# Revit family: IS_ConceptAir_Multiproduct_BIM_GB_E0826;E0827;E0828;E0829
name_source: partatom
category: Plumbing Fixtures
revit_build: Autodesk Revit MEP 2014 (Build: 20140709_2115(x64)
units: mm (PartAtom-declared; Revit-internal decimal feet)

## types (24) — shared parameters
Accessories = www.idealspec.co.uk
AreaUnits = millimeters
Assembly Code = C1030200
AssetType = Fixed
BREEAM = No
Brand = IdealStandard
Default Elevation = 800 mm  [stored 2.62467 ft]
DurationUnit = year
ECA = No
ExpectedLife = 30
IfcExportAs = IfcFurnitureType
IfcExportType = USERDEFINED
InstallationInstructions = www.idealspec.co.uk/resources.html
LinearUnits = millimeters
ManufacturerURL = www.idealspec.co.uk
Material = Laquered MDF
NBSDescription = Bathroom integrated duct work
NBSReference = 45-35-72/320
NettWeight = 0 Kg
NominalDepth = 440 mm  [stored 1.44357 ft]
NominalHeight = 517 mm  [stored 1.69619 ft]
NominalLength = 440 mm  [stored 1.44357 ft]
Shape = Rectangular
Space = Internal
SpareParts = www.fastpart-spares.co.uk
TMV3 = No
URL = www.idealspec.co.uk
Uniclass2 = Pr_40_30_78_04
Version = 1
VolumeUnits = Litres
WRAS = No
WarrantyDescription = Manufacturers warranty
WarrantyDurationParts = 5
WarrantyDurationUnit = year
WaterEfficientProduct = No
zero-valued in all types: CWFU, Cost, HWFU, WFU

## per-type parameters (varying)
| type | 1Drawer | 2Drawer | BIMObjectName | Color | Description | Features | Finish | InnerColour | MainColor | MainColour | Model | ModelNumber | ModelReference | Name | NominalWidth | ProductInformation | Size |
| E0828B2 - 100CM Wall Hung Vanity Unit 1 Drawer with open shelf Gls White + Matt White | Yes | No | ISI_IdealStandard_Furniture_ConceptAir_E0828B2 | White | Concept Air 100 cm Wall Hung Vanity Unit 1 Drawer with open shelf Gls White + Matt White | 100 cm Wall Hung Vanity Unit 1 Drawer with open shelf Gls White + Matt White | White | ISI_IdealStandard_Laminate_White_Render | White | ISI_IdealStandard_Laminate_White_Render | E0828B2 | E0828B2 | Concept Air 100 cm Wall Hung Vanity Unit 1 Drawer with open shelf Gls White + Matt White | Furniture_ConceptAir_E0828B2_IdealStandard | 1000 mm  [stored 3.28084 ft] | www.idealspec.co.uk/assets/datasheet/E0828B2 | 517 x 440 x 1000 mm |
| E0828UK - 100CM Wall Hung Vanity Unit 1 Drawer with open shelf Wood Light Brown + Matt Light Brown | Yes | No | ISI_IdealStandard_Furniture_ConceptAir_E0828UK | Wood brown | Concept Air 100 cm Wall Hung Vanity Unit 1 Drawer with open shelf Wood Light Brown + Matt Light Brown | 100 cm Wall Hung Vanity Unit 1 Drawer with open shelf Wood Light Brown + Matt Light Brown | Wood brown | ISI_IdealStandard_Furniture_WoodLightBrown_Render | Wood brown | ISI_IdealStandard_Furniture_WoodLightBrown_Render | E0828UK | E0828UK | Concept Air 100 cm Wall Hung Vanity Unit 1 Drawer with open shelf Wood Light Brown + Matt Light Brown | Furniture_ConceptAir_E0828UK_IdealStandard | 1000 mm  [stored 3.28084 ft] | www.idealspec.co.uk/assets/datasheet/E0828UK | 517 x 440 x 1000 mm |
| E0828PS - 100CM Wall Hung Vanity Unit 1 Drawer with open shelf Wood Light Grey + Matt White | Yes | No | ISI_IdealStandard_Furniture_ConceptAir_E0828PS | Wood grey | Concept Air 100 cm Wall Hung Vanity Unit 1 Drawer with open shelf Wood Light Grey + Matt White | 100 cm Wall Hung Vanity Unit 1 Drawer with open shelf Wood Light Grey + Matt White | Wood grey | ISI_IdealStandard_Laminate_White_Render | Wood grey | ISI_IdealStandard_Furniture_WoodLightGrey_Render | E0828PS | E0828PS | Concept Air 100 cm Wall Hung Vanity Unit 1 Drawer with open shelf Wood Light Grey + Matt White | Furniture_ConceptAir_E0828PS_IdealStandard | 1000 mm  [stored 3.28084 ft] | www.idealspec.co.uk/assets/datasheet/E0828PS | 517 x 440 x 1000 mm |
| E0828KN - 100CM Wall Hung Vanity Unit 1 Drawer with open shelf Gls White + Matt Light Grey | Yes | No | ISI_IdealStandard_Furniture_ConceptAir_E0828KN | White | Concept Air 100 cm Wall Hung Vanity Unit 1 Drawer with open shelf Gls White + Matt Light Grey | 100 cm Wall Hung Vanity Unit 1 Drawer with open shelf Gls White + Matt Light Grey | White | ISI_IdealStandard_Furniture_Grey_Render | White | ISI_IdealStandard_Laminate_White_Render | E0828KN | E0828KN | Concept Air 100 cm Wall Hung Vanity Unit 1 Drawer with open shelf Gls White + Matt Light Grey | Furniture_ConceptAir_E0828KN_IdealStandard | 1000 mm  [stored 3.28084 ft] | www.idealspec.co.uk/assets/datasheet/E0828KN | 517 x 440 x 1000 mm |
| E0827EQ - 80CM Wall Hung Vanity Unit 1 Drawer with open shelf Gls Light Grey + Matt White | Yes | No | ISI_IdealStandard_Furniture_ConceptAir_E0827EQ | Grey | Concept Air 80 cm Wall Hung Vanity Unit 1 Drawer with open shelf Gls Light Grey + Matt White | 80 cm Wall Hung Vanity Unit 1 Drawer with open shelf Gls Light Grey + Matt White | Grey | ISI_IdealStandard_Laminate_White_Render | Grey | ISI_IdealStandard_Furniture_Grey_Render | E0827EQ | E0827EQ | Concept Air 80 cm Wall Hung Vanity Unit 1 Drawer with open shelf Gls Light Grey + Matt White | Furniture_ConceptAir_E0827EQ_IdealStandard | 800 mm  [stored 2.62467 ft] | www.idealspec.co.uk/assets/datasheet/E0827EQ | 517 x 440 x 800 mm |
| E0827UK - 80CM Wall Hung Vanity Unit 1 Drawer with open shelf Wood Light Brown + Matt Light Brown | Yes | No | ISI_IdealStandard_Furniture_ConceptAir_E0827UK | Wood brown | Concept Air 80 cm Wall Hung Vanity Unit 1 Drawer with open shelf Wood Light Brown + Matt Light Brown | 80 cm Wall Hung Vanity Unit 1 Drawer with open shelf Wood Light Brown + Matt Light Brown | Wood brown | ISI_IdealStandard_Furniture_WoodLightBrown_Render | Wood brown | ISI_IdealStandard_Furniture_WoodLightBrown_Render | E0827UK | E0827UK | Concept Air 80 cm Wall Hung Vanity Unit 1 Drawer with open shelf Wood Light Brown + Matt Light Brown | Furniture_ConceptAir_E0827UK_IdealStandard | 800 mm  [stored 2.62467 ft] | www.idealspec.co.uk/assets/datasheet/E0827UK | 517 x 440 x 800 mm |
| E0827PS - 80CM Wall Hung Vanity Unit 1 Drawer with open shelf Wood Light Grey + Matt White | Yes | No | ISI_IdealStandard_Furniture_ConceptAir_E0827PS | Wood grey | Concept Air 80 cm Wall Hung Vanity Unit 1 Drawer with open shelf Wood Light Grey + Matt White | 80 cm Wall Hung Vanity Unit 1 Drawer with open shelf Wood Light Grey + Matt White | Wood grey | ISI_IdealStandard_Laminate_White_Render | Wood grey | ISI_IdealStandard_Furniture_WoodLightGrey_Render | E0827PS | E0827PS | Concept Air 80 cm Wall Hung Vanity Unit 1 Drawer with open shelf Wood Light Grey + Matt White | Furniture_ConceptAir_E0827PS_IdealStandard | 800 mm  [stored 2.62467 ft] | www.idealspec.co.uk/assets/datasheet/E0827PS | 517 x 440 x 800 mm |
| E0827KN - 80CM Wall Hung Vanity Unit 1 Drawer with open shelf Gls White + Matt Light Grey | Yes | No | ISI_IdealStandard_Furniture_ConceptAir_E0827KN | White | Concept Air 80 cm Wall Hung Vanity Unit 1 Drawer with open shelf Gls White + Matt Light Grey | 80 cm Wall Hung Vanity Unit 1 Drawer with open shelf Gls White + Matt Light Grey | White | ISI_IdealStandard_Furniture_Grey_Render | White | ISI_IdealStandard_Laminate_White_Render | E0827KN | E0827KN | Concept Air 80 cm Wall Hung Vanity Unit 1 Drawer with open shelf Gls White + Matt Light Grey | Furniture_ConceptAir_E0827KN_IdealStandard | 800 mm  [stored 2.62467 ft] | www.idealspec.co.uk/assets/datasheet/E0827KN | 517 x 440 x 800 mm |
| E0828EQ - 100CM Wall Hung Vanity Unit 1 Drawer with open shelf Gls Light Grey + Matt White | Yes | No | ISI_IdealStandard_Furniture_ConceptAir_E0828EQ | Grey | Concept Air 100 cm Wall Hung Vanity Unit 1 Drawer with open shelf Gls Light Grey + Matt White | 100 cm Wall Hung Vanity Unit 1 Drawer with open shelf Gls Light Grey + Matt White | Grey | ISI_IdealStandard_Laminate_White_Render | Grey | ISI_IdealStandard_Furniture_Grey_Render | E0828EQ | E0828EQ | Concept Air 100 cm Wall Hung Vanity Unit 1 Drawer with open shelf Gls Light Grey + Matt White | Furniture_ConceptAir_E0828EQ_IdealStandard | 1000 mm  [stored 3.28084 ft] | www.idealspec.co.uk/assets/datasheet/E0828EQ | 517 x 440 x 1000 mm |
| E0827B2 - 80CM Wall Hung Vanity Unit 1 Drawer with open shelf Gls White + Matt White | Yes | No | ISI_IdealStandard_Furniture_ConceptAir_E0827B2 | White | Concept Air 80 cm Wall Hung Vanity Unit 1 Drawer with open shelf Gls White + Matt White | 80 cm Wall Hung Vanity Unit 1 Drawer with open shelf Gls White + Matt White | White | ISI_IdealStandard_Laminate_White_Render | White | ISI_IdealStandard_Laminate_White_Render | E0827B2 | E0827B2 | Concept Air 80 cm Wall Hung Vanity Unit 1 Drawer with open shelf Gls White + Matt White | Furniture_ConceptAir_E0827B2_IdealStandard | 800 mm  [stored 2.62467 ft] | www.idealspec.co.uk/assets/datasheet/E0827B2 | 517 x 440 x 800 mm |
| E0826UK - 60CM Wall Hung Vanity Unit 1 Drawer with open shelf Wood Light Brown + Matt Light Brown | Yes | No | ISI_IdealStandard_Furniture_ConceptAir_E0826UK | Wood brown | Concept Air 60 cm Wall Hung Vanity Unit 1 Drawer with open shelf Wood Light Brown + Matt Light Brown | 60 cm Wall Hung Vanity Unit 1 Drawer with open shelf Wood Light Brown + Matt Light Brown | Wood brown | ISI_IdealStandard_Furniture_WoodLightBrown_Render | Wood brown | ISI_IdealStandard_Furniture_WoodLightBrown_Render | E0826UK | E0826UK | Concept Air 60 cm Wall Hung Vanity Unit 1 Drawer with open shelf Wood Light Brown + Matt Light Brown | Furniture_ConceptAir_E0826UK_IdealStandard | 600 mm | www.idealspec.co.uk/assets/datasheet/E0826UK | 517 x 440 x 600 mm |
| E0826PS - 60CM Wall Hung Vanity Unit 1 Drawer with open shelf Wood Light Grey + Matt White | Yes | No | ISI_IdealStandard_Furniture_ConceptAir_E0826PS | Wood grey | Concept Air 60 cm Wall Hung Vanity Unit 1 Drawer with open shelf Wood Light Grey + Matt White | 60 cm Wall Hung Vanity Unit 1 Drawer with open shelf Wood Light Grey + Matt White | Wood grey | ISI_IdealStandard_Laminate_White_Render | Wood grey | ISI_IdealStandard_Furniture_WoodLightGrey_Render | E0826PS | E0826PS | Concept Air 60 cm Wall Hung Vanity Unit 1 Drawer with open shelf Wood Light Grey + Matt White | Furniture_ConceptAir_E0826PS_IdealStandard | 600 mm | www.idealspec.co.uk/assets/datasheet/E0826PS | 517 x 440 x 600 mm |
| E0826KN - 60CM Wall Hung Vanity Unit 1 Drawer with open shelf Gls White + Matt Light Grey | Yes | No | ISI_IdealStandard_Furniture_ConceptAir_E0826KN | White | Concept Air 60 cm Wall Hung Vanity Unit 1 Drawer with open shelf Gls White + Matt Light Grey | 60 cm Wall Hung Vanity Unit 1 Drawer with open shelf Gls White + Matt Light Grey | White | ISI_IdealStandard_Furniture_Grey_Render | White | ISI_IdealStandard_Laminate_White_Render | E0826KN | E0826KN | Concept Air 60 cm Wall Hung Vanity Unit 1 Drawer with open shelf Gls White + Matt Light Grey | Furniture_ConceptAir_E0826KN_IdealStandard | 600 mm | www.idealspec.co.uk/assets/datasheet/E0826KN | 517 x 440 x 600 mm |
| E0826EQ - 60CM Wall Hung Vanity Unit 1 Drawer with open shelf Gls Light Grey + Matt White | Yes | No | ISI_IdealStandard_Furniture_ConceptAir_E0826EQ | Grey | Concept Air 60 cm Wall Hung Vanity Unit 1 Drawer with open shelf Gls Light Grey + Matt White | 60 cm Wall Hung Vanity Unit 1 Drawer with open shelf Gls Light Grey + Matt White | Grey | ISI_IdealStandard_Laminate_White_Render | Grey | ISI_IdealStandard_Furniture_Grey_Render | E0826EQ | E0826EQ | Concept Air 60 cm Wall Hung Vanity Unit 1 Drawer with open shelf Gls Light Grey + Matt White | Furniture_ConceptAir_E0826EQ_IdealStandard | 600 mm | www.idealspec.co.uk/assets/datasheet/E0826EQ | 517 x 440 x 600 mm |
| E0826B2 - 60CM Wall Hung Vanity Unit 1 Drawer with open shelf Gls White + Matt White | Yes | No | ISI_IdealStandard_Furniture_ConceptAir_E0826B2 | White | Concept Air 60 cm Wall Hung Vanity Unit 1 Drawer with open shelf Gls White + Matt White | 60 cm Wall Hung Vanity Unit 1 Drawer with open shelf Gls White + Matt White | White | ISI_IdealStandard_Laminate_White_Render | White | ISI_IdealStandard_Laminate_White_Render | E0826B2 | E0826B2 | Concept Air 60 cm Wall Hung Vanity Unit 1 Drawer with open shelf Gls White + Matt White | Furniture_ConceptAir_E0826B2_IdealStandard | 600 mm | www.idealspec.co.uk/assets/datasheet/E0826B2 | 517 x 440 x 600 mm |
| E0829B2 - 120CM Wall Hung Vanity Unit 2 Drawer with open shelf Gls White + Matt White | No | Yes | ISI_IdealStandard_Furniture_ConceptAir_E0829B2 | White | Concept Air 120 cm Wall Hung Vanity Unit 2 Drawer with open shelf Gls White + Matt White | 120 cm Wall Hung Vanity Unit 2 Drawer with open shelf Gls White + Matt White | White | ISI_IdealStandard_Laminate_White_Render | White | ISI_IdealStandard_Laminate_White_Render | E0829B2 | E0829B2 | Concept Air 120 cm Wall Hung Vanity Unit 2 Drawer with open shelf Gls White + Matt White | Furniture_ConceptAir_E0829B2_IdealStandard | 1200 mm | www.idealspec.co.uk/assets/datasheet/E0829B2 | 517 x 440 x 1200 mm |
| E0829EQ - 120CM Wall Hung Vanity Unit 2 Drawer with open shelf Gls Light Grey + Matt White | No | Yes | ISI_IdealStandard_Furniture_ConceptAir_E0829EQ | Grey | Concept Air 120 cm Wall Hung Vanity Unit 2 Drawer with open shelf Gls Light Grey + Matt White | 120 cm Wall Hung Vanity Unit 2 Drawer with open shelf Gls Light Grey + Matt White | Grey | ISI_IdealStandard_Laminate_White_Render | Grey | ISI_IdealStandard_Furniture_Grey_Render | E0829EQ | E0829EQ | Concept Air 120 cm Wall Hung Vanity Unit 2 Drawer with open shelf Gls Light Grey + Matt White | Furniture_ConceptAir_E0829EQ_IdealStandard | 1200 mm | www.idealspec.co.uk/assets/datasheet/E0829EQ | 517 x 440 x 1200 mm |
| E0829KN - 120CM Wall Hung Vanity Unit 2 Drawer with open shelf Gls White + Matt Light Grey | No | Yes | ISI_IdealStandard_Furniture_ConceptAir_E0829KN | White | Concept Air 120 cm Wall Hung Vanity Unit 2 Drawer with open shelf Gls White + Matt Light Grey | 120 cm Wall Hung Vanity Unit 2 Drawer with open shelf Gls White + Matt Light Grey | White | ISI_IdealStandard_Furniture_Grey_Render | White | ISI_IdealStandard_Laminate_White_Render | E0829KN | E0829KN | Concept Air 120 cm Wall Hung Vanity Unit 2 Drawer with open shelf Gls White + Matt Light Grey | Furniture_ConceptAir_E0829KN_IdealStandard | 1200 mm | www.idealspec.co.uk/assets/datasheet/E0829KN | 517 x 440 x 1200 mm |
| E0829PS - 120CM Wall Hung Vanity Unit 2 Drawer with open shelf Wood Light Grey + Matt White | No | Yes | ISI_IdealStandard_Furniture_ConceptAir_E0829PS | Wood grey | Concept Air 120 cm Wall Hung Vanity Unit 2 Drawer with open shelf Wood Light Grey + Matt White | 120 cm Wall Hung Vanity Unit 2 Drawer with open shelf Wood Light Grey + Matt White | Wood grey | ISI_IdealStandard_Laminate_White_Render | Wood grey | ISI_IdealStandard_Furniture_WoodLightGrey_Render | E0829PS | E0829PS | Concept Air 120 cm Wall Hung Vanity Unit 2 Drawer with open shelf Wood Light Grey + Matt White | Furniture_ConceptAir_E0829PS_IdealStandard | 1200 mm | www.idealspec.co.uk/assets/datasheet/E0829PS | 517 x 440 x 1200 mm |
| E0829UK - 120CM Wall Hung Vanity Unit 2 Drawer with open shelf Wood Light Brown + Matt Light Brown | No | Yes | ISI_IdealStandard_Furniture_ConceptAir_E0829UK | Wood brown | Concept Air 120 cm Wall Hung Vanity Unit 2 Drawer with open shelf Wood Light Brown + Matt Light Brown | 120 cm Wall Hung Vanity Unit 2 Drawer with open shelf Wood Light Brown + Matt Light Brown | Wood brown | ISI_IdealStandard_Furniture_WoodLightBrown_Render | Wood brown | ISI_IdealStandard_Furniture_WoodLightBrown_Render | E0829UK | E0829UK | Concept Air 120 cm Wall Hung Vanity Unit 2 Drawer with open shelf Wood Light Brown + Matt Light Brown | Furniture_ConceptAir_E0829UK_IdealStandard | 1200 mm | www.idealspec.co.uk/assets/datasheet/E0829UK | 517 x 440 x 1200 mm |
| E0829VY - 120CM Wall Hung Vanity Unit 2 Drawer with open shelf Matt Dark Brown + Matt White | No | Yes | ISI_IdealStandard_Furniture_ConceptAir_E0829VY | Dark brown | Concept Air 120 cm Wall Hung Vanity Unit 2 Drawer with open shelf Matt Dark Brown + Matt White | 120 cm Wall Hung Vanity Unit 2 Drawer with open shelf Matt Dark Brown + Matt White | Dark brown | ISI_IdealStandard_Laminate_White_Render | Dark brown | ISI_IdealStandard_Furniture_DarkBrown_Render | E0829VY | E0829VY | Concept Air 120 cm Wall Hung Vanity Unit 2 Drawer with open shelf Gls Dark Brown + Matt White | Furniture_ConceptAir_E0829VY_IdealStandard | 1200 mm | www.idealspec.co.uk/assets/datasheet/E0829VY | 517 x 440 x 1200 mm |
| E0826VY - 60CM Wall Hung Vanity Unit 1 Drawer with open shelf Matt Dark Brown + Matt White | Yes | No | ISI_IdealStandard_Furniture_ConceptAir_E0826VY | Dark brown | Concept Air 60 cm Wall Hung Vanity Unit 1 Drawer with open shelf Matt Dark Brown + Matt White | 60 cm Wall Hung Vanity Unit 1 Drawer with open shelf Matt Dark Brown + Matt White | Dark brown | ISI_IdealStandard_Laminate_White_Render | Dark brown | ISI_IdealStandard_Furniture_DarkBrown_Render | E0826VY | E0826VY | Concept Air 60 cm Wall Hung Vanity Unit 1 Drawer with open shelf Gls Dark Brown + Matt White | Furniture_ConceptAir_E0826VY_IdealStandard | 600 mm | www.idealspec.co.uk/assets/datasheet/E0826VY | 517 x 440 x 600 mm |
| E0827VY - 80CM Wall Hung Vanity Unit 1 Drawer with open shelf Matt Dark Brown + Matt White | Yes | No | ISI_IdealStandard_Furniture_ConceptAir_E0827VY | Dark brown | Concept Air 80 cm Wall Hung Vanity Unit 1 Drawer with open shelf Matt Dark Brown + Matt White | 80 cm Wall Hung Vanity Unit 1 Drawer with open shelf Matt Dark Brown + Matt White | Dark brown | ISI_IdealStandard_Laminate_White_Render | Dark brown | ISI_IdealStandard_Furniture_DarkBrown_Render | E0827VY | E0827VY | Concept Air 80 cm Wall Hung Vanity Unit 1 Drawer with open shelf Gls Dark Brown + Matt White | Furniture_ConceptAir_E0827VY_IdealStandard | 800 mm  [stored 2.62467 ft] | www.idealspec.co.uk/assets/datasheet/E0827VY | 517 x 440 x 800 mm |
| E0828VY - 100CM Wall Hung Vanity Unit 1 Drawer with open shelf Matt Dark Brown + Matt White | Yes | No | ISI_IdealStandard_Furniture_ConceptAir_E0828VY | Dark brown | Concept Air 100 cm Wall Hung Vanity Unit 1 Drawer with open shelf Matt Dark Brown + Matt White | 100 cm Wall Hung Vanity Unit 1 Drawer with open shelf Matt Dark Brown + Matt White | Dark brown | ISI_IdealStandard_Laminate_White_Render | Dark brown | ISI_IdealStandard_Furniture_DarkBrown_Render | E0828VY | E0828VY | Concept Air 100 cm Wall Hung Vanity Unit 1 Drawer with open shelf Gls Dark Brown + Matt White | Furniture_ConceptAir_E0828VY_IdealStandard | 1000 mm  [stored 3.28084 ft] | www.idealspec.co.uk/assets/datasheet/E0828VY | 517 x 440 x 1000 mm |

note: [stored X ft] marks values corroborated as IEEE doubles in the binary element streams (Revit-internal decimal feet)

## geometry (parser evidence)
native form markers: Sweep x2
no freeform markers — native parametric forms only
